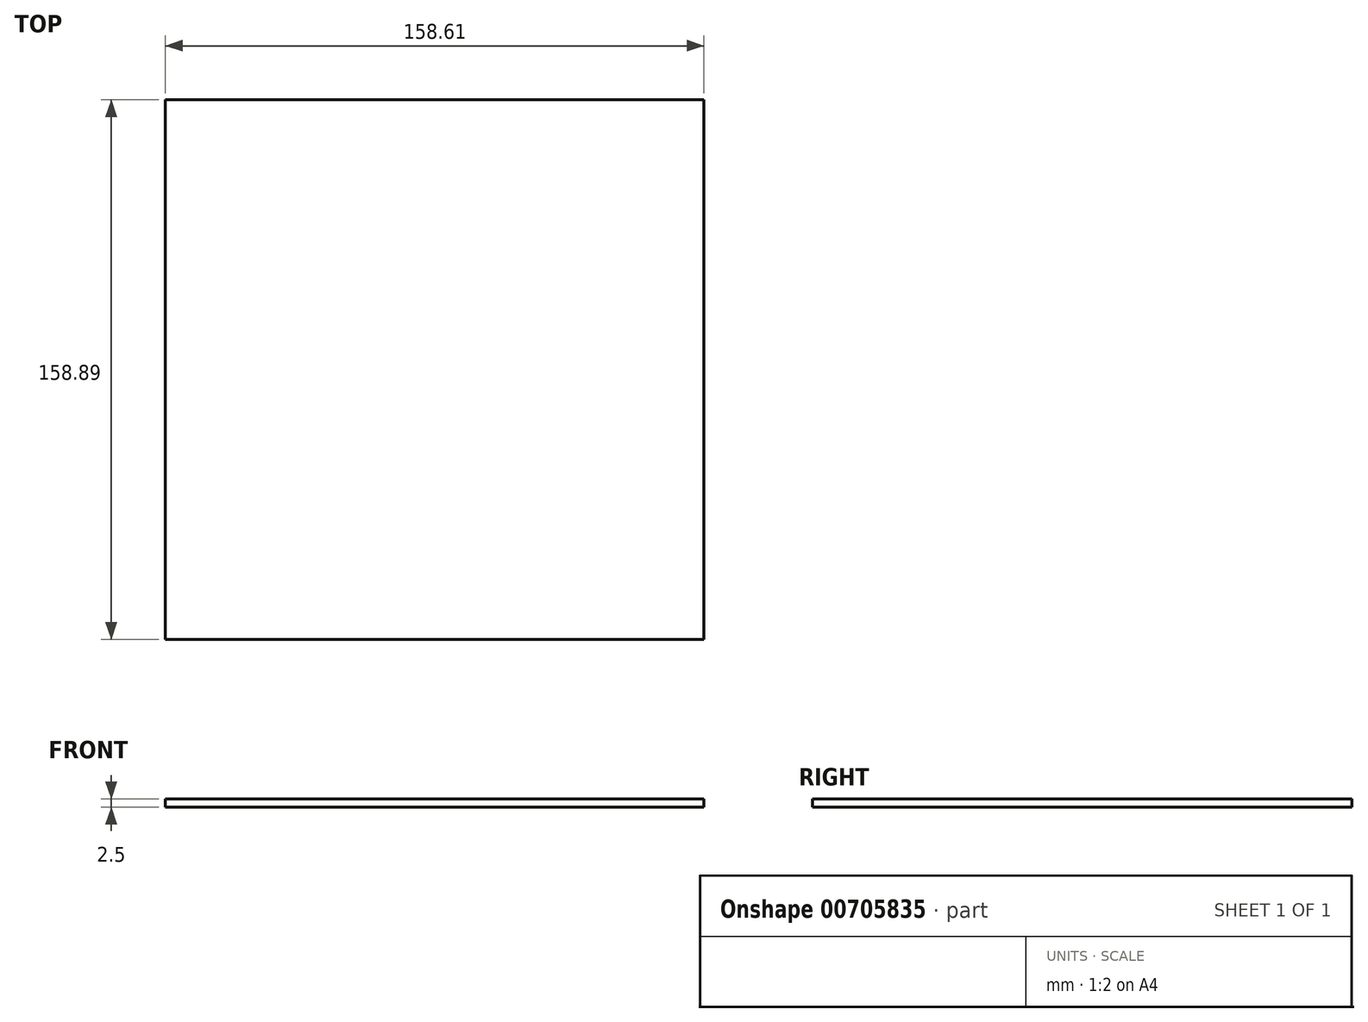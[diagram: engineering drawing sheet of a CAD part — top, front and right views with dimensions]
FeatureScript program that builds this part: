
annotation { "Feature Type Name" : "Feature", "Feature Type Description" : "" }
export const myFeature = defineFeature(function(context is Context, id is Id, definition is map)
    precondition{}
    {
        {
            var Q0;
            Q0=qCreatedBy(makeId("Top.planeOp"),FACE);
            var sketch = newSketch(context, id + "F0", { "sketchPlane" : qUnion([Q0])});
            skLineSegment(sketch, "E0.bottom", {"start": v(-83.38, 81.68) * mm, "end": v(75.23, 81.68) * mm});
            skLineSegment(sketch, "E0.top", {"start": v(-83.38, -77.21) * mm, "end": v(75.23, -77.21) * mm});
            skLineSegment(sketch, "E0.left", {"start": v(-83.38, 81.68) * mm, "end": v(-83.38, -77.21) * mm});
            skLineSegment(sketch, "E0.right", {"start": v(75.23, 81.68) * mm, "end": v(75.23, -77.21) * mm});
            skSolve(sketch);
        }
        {
            var Q0;
            Q0 = qSketchRegion(id + "F0", true);
            extrude(context, id + "F1", {"entities" : qUnion([Q0]), "endBound" : BoundingType.SYMMETRIC, "depth" : 2.5 * mm, "offsetDistance" : 25.4 * mm});
        }
    });
